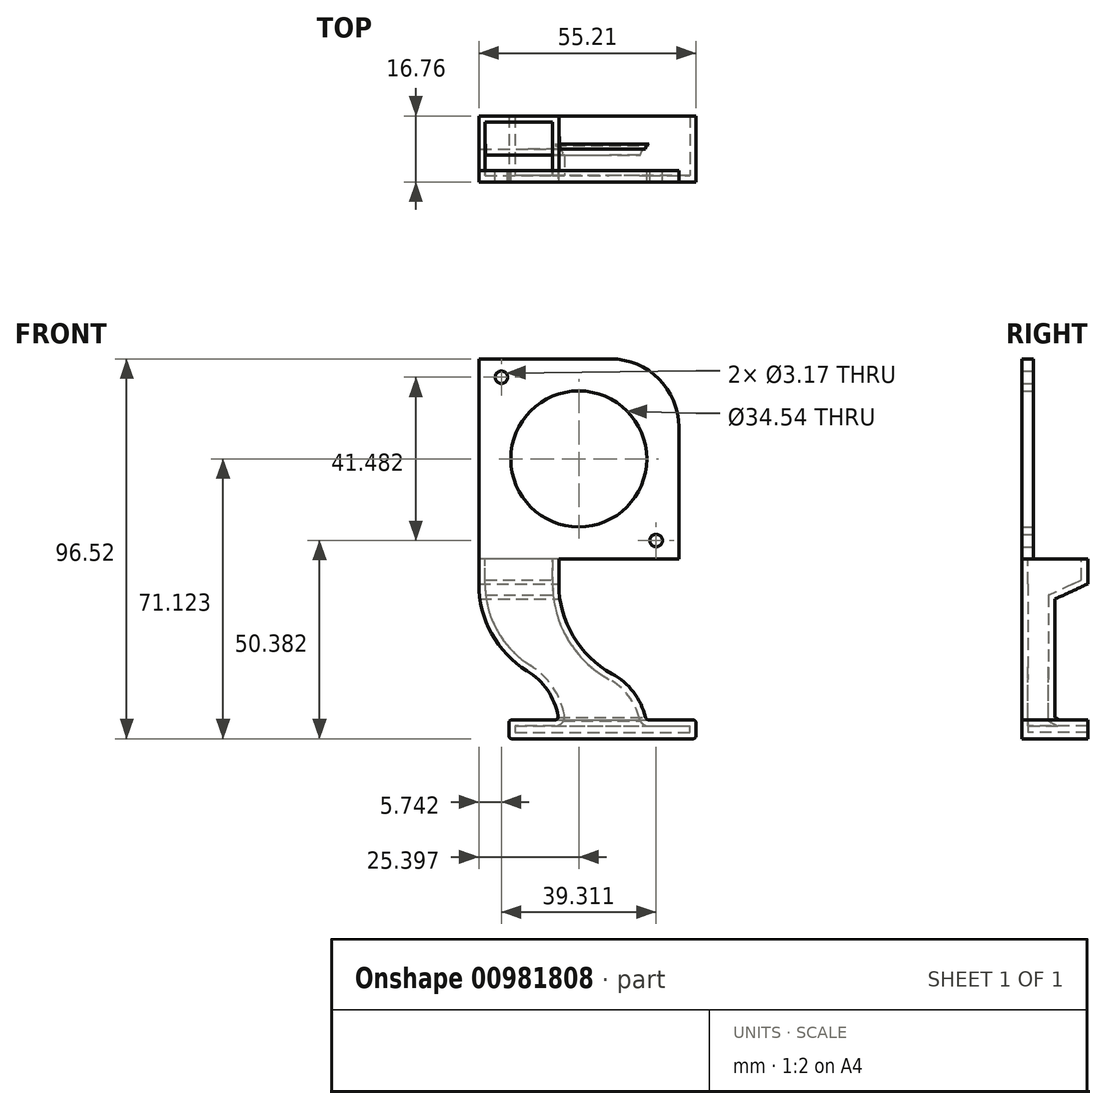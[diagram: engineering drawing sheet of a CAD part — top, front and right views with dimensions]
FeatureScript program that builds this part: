
annotation { "Feature Type Name" : "Feature", "Feature Type Description" : "" }
export const myFeature = defineFeature(function(context is Context, id is Id, definition is map)
    precondition{}
    {
        {
            var Q0;
            Q0=qCreatedBy(makeId("Front.planeOp"),FACE);
            var sketch = newSketch(context, id + "F0", { "sketchPlane" : qUnion([Q0])});
            skLineSegment(sketch, "E0", {"start": v(-842.3, 183.05) * mm, "end": v(-808.77, 183.05) * mm});
            skLineSegment(sketch, "E1", {"start": v(-791.5, 165.78) * mm, "end": v(-791.5, 132.25) * mm});
            skLineSegment(sketch, "E2", {"start": v(-791.5, 132.25) * mm, "end": v(-842.3, 132.25) * mm});
            skLineSegment(sketch, "E3", {"start": v(-842.3, 132.25) * mm, "end": v(-842.3, 183.05) * mm});
            skCircle(sketch, "E4", {"center": v(-816.9, 157.65) * mm, "radius": 17.27 * mm});
            skPoint(sketch, "E4.centerSnap0", {"position": v(-791.5, 157.65) * mm});
            skPoint(sketch, "E4.centerSnap1", {"position": v(-816.9, 132.25) * mm});
            skCircle(sketch, "E5", {"center": v(-836.56, 178.4) * mm, "radius": 1.59 * mm});
            skCircle(sketch, "E6", {"center": v(-797.25, 136.91) * mm, "radius": 1.59 * mm});
            skPoint(sketch, "E7.visualSharp", {"position": v(-791.5, 183.05) * mm});
            skArc(sketch, "E7.filletArc", {"start": v(-791.5, 165.78) * mm, "mid": v(-796.56, 178) * mm, "end": v(-808.77, 183.05) * mm});
            skSolve(sketch);
        }
        {
            var Q0;
            Q0 = qSketchRegion(id + "F0", true);
            extrude(context, id + "F1", {"entities" : qUnion([Q0]), "depth" : 2.92 * mm, "offsetDistance" : 25.4 * mm});
        }
        {
            var Q0;
            Q0=makeQuery(id+"F1.opExtrude","SWEPT_FACE",FACE,{"disambiguationData":[OSD([sQuery(id+"F0.wireOp",EDGE,"E3")])]});
            var sketch = newSketch(context, id + "F2", { "sketchPlane" : qUnion([Q0])});
            skLineSegment(sketch, "E8.bottom", {"start": v(2.92, 132.25) * mm, "end": v(-13.84, 132.25) * mm});
            skLineSegment(sketch, "E8.left", {"start": v(2.92, 132.25) * mm, "end": v(2.92, 125.9) * mm});
            skPoint(sketch, "E9.first.point", {"position": v(2.92, 125.9) * mm});
            skLineSegment(sketch, "E10", {"start": v(2.92, 125.9) * mm, "end": v(-13.84, 125.9) * mm});
            skLineSegment(sketch, "E11", {"start": v(-13.84, 125.9) * mm, "end": v(-13.84, 132.25) * mm});
            skSolve(sketch);
        }
        {
            var Q0;
            {var subQ0=sQuery(id+"F2.wireOp",EDGE,"E8.left");Q0=makeQuery(id+"F2.imprint","IMPRINT",FACE,{"disambiguationData":[TD([[makeQuery(id+"F2.imprint","IMPRINT",EDGE,{"derivedFrom":subQ0}),-1.0]])]});}
            extrude(context, id + "F3", {"entities" : qUnion([Q0]), "operationType" : NewBodyOperationType.ADD, "depth" : -20.32 * mm, "offsetDistance" : 25.4 * mm});
        }
        {
            var Q0;
            Q0=makeQuery(id+"F3.boolean.opBoolean","MERGE",FACE,{"derivedFrom":[makeQuery(id+"F1.opExtrude","CAP_FACE",FACE,{"disambiguationData":[OSD([sQuery(id+"F0.wireOp",EDGE,"E0"),sQuery(id+"F0.wireOp",EDGE,"E1"),sQuery(id+"F0.wireOp",EDGE,"E2"),sQuery(id+"F0.wireOp",EDGE,"E3"),sQuery(id+"F0.wireOp",EDGE,"E4"),sQuery(id+"F0.wireOp",EDGE,"E5"),sQuery(id+"F0.wireOp",EDGE,"E6"),sQuery(id+"F0.wireOp",EDGE,"E7.filletArc")])],"isStart":false}),makeQuery(id+"F3.opExtrude","SWEPT_FACE",FACE,{"disambiguationData":[OSD([sQuery(id+"F2.wireOp",EDGE,"E8.left")])]})]});
            var sketch = newSketch(context, id + "F4", { "sketchPlane" : qUnion([Q0])});
            skArc(sketch, "E12", {"start": v(-842.3, 125.9) * mm, "mid": v(-839.02, 113.25) * mm, "end": v(-830, 103.78) * mm});
            skArc(sketch, "E13", {"start": v(-821.98, 125.9) * mm, "mid": v(-818.34, 112.62) * mm, "end": v(-808.43, 103.06) * mm});
            skLineSegment(sketch, "E14", {"start": v(-821.98, 91.36) * mm, "end": v(-821.98, 90.34) * mm});
            skLineSegment(sketch, "E15", {"start": v(-799.8, 91.36) * mm, "end": v(-799.76, 91.2) * mm});
            skPoint(sketch, "E16.visualSharp", {"position": v(-821.98, 100.5) * mm});
            skArc(sketch, "E16.filletArc", {"start": v(-822.14, 92.35) * mm, "mid": v(-824.87, 98.89) * mm, "end": v(-830, 103.78) * mm});
            skPoint(sketch, "E17.visualSharp", {"position": v(-801.66, 100.5) * mm});
            skArc(sketch, "E17.filletArc", {"start": v(-799.94, 92) * mm, "mid": v(-803.02, 98.42) * mm, "end": v(-808.43, 103.06) * mm});
            skLineSegment(sketch, "E18", {"start": v(-822.96, 91.36) * mm, "end": v(-833.85, 91.36) * mm});
            skLineSegment(sketch, "E19", {"start": v(-799.13, 91.36) * mm, "end": v(-787.93, 91.36) * mm});
            skLineSegment(sketch, "E20", {"start": v(-787.93, 86.53) * mm, "end": v(-833.85, 86.53) * mm});
            skLineSegment(sketch, "E21", {"start": v(-834.68, 87.36) * mm, "end": v(-834.68, 90.53) * mm});
            skLineSegment(sketch, "E22", {"start": v(-787.1, 90.53) * mm, "end": v(-787.1, 87.36) * mm});
            skPoint(sketch, "E23.visualSharp", {"position": v(-821.98, 91.36) * mm});
            skArc(sketch, "E23.filletArc", {"start": v(-822.96, 91.36) * mm, "mid": v(-822.32, 91.66) * mm, "end": v(-822.14, 92.35) * mm});
            skPoint(sketch, "E24.visualSharp", {"position": v(-799.8, 91.36) * mm});
            skArc(sketch, "E24.filletArc", {"start": v(-799.94, 92) * mm, "mid": v(-799.64, 91.54) * mm, "end": v(-799.13, 91.36) * mm});
            skPoint(sketch, "E25.visualSharp", {"position": v(-787.1, 91.36) * mm});
            skArc(sketch, "E25.filletArc", {"start": v(-787.1, 90.53) * mm, "mid": v(-787.34, 91.12) * mm, "end": v(-787.93, 91.36) * mm});
            skPoint(sketch, "E26.visualSharp", {"position": v(-787.1, 86.53) * mm});
            skArc(sketch, "E26.filletArc", {"start": v(-787.93, 86.53) * mm, "mid": v(-787.34, 86.78) * mm, "end": v(-787.1, 87.36) * mm});
            skPoint(sketch, "E27.visualSharp", {"position": v(-834.68, 91.36) * mm});
            skArc(sketch, "E27.filletArc", {"start": v(-833.85, 91.36) * mm, "mid": v(-834.44, 91.12) * mm, "end": v(-834.68, 90.53) * mm});
            skPoint(sketch, "E28.visualSharp", {"position": v(-834.68, 86.53) * mm});
            skArc(sketch, "E28.filletArc", {"start": v(-834.68, 87.36) * mm, "mid": v(-834.44, 86.78) * mm, "end": v(-833.85, 86.53) * mm});
            skLineSegment(sketch, "E29", {"start": v(-842.3, 125.9) * mm, "end": v(-821.98, 125.9) * mm});
            skSolve(sketch);
        }
        {
            var Q0;
            Q0=makeQuery(id+"F4.imprint","IMPRINT",FACE,{"disambiguationData":[TD([[makeQuery(id+"F4.imprint","IMPRINT",EDGE,{"derivedFrom":sQuery(id+"F4.wireOp",EDGE,"E12")}),1.0]])]});
            var Q1;
            Q1=makeQuery(id+"F3.opExtrude","SWEPT_FACE",FACE,{"disambiguationData":[OSD([sQuery(id+"F2.wireOp",EDGE,"E11")])]});
            extrude(context, id + "F5", {"entities" : qUnion([Q0]), "operationType" : NewBodyOperationType.ADD, "endBound" : BoundingType.UP_TO_SURFACE, "oppositeDirection" : true, "depth" : 25.4 * mm, "endBoundEntityFace" : qUnion([Q1]), "offsetDistance" : 25.4 * mm});
        }
        {
            var Q0;
            Q0=makeQuery(id+"F5.opExtrude","SWEPT_FACE",FACE,{"disambiguationData":[OSD([sQuery(id+"F4.wireOp",EDGE,"E22")])]});
            var sketch = newSketch(context, id + "F6", { "sketchPlane" : qUnion([Q0])});
            skLineSegment(sketch, "E30", {"start": v(13.84, 125.9) * mm, "end": v(5.46, 122) * mm});
            skLineSegment(sketch, "E31", {"start": v(5.46, 122) * mm, "end": v(5.46, 92) * mm});
            skLineSegment(sketch, "E32", {"start": v(5.46, 92) * mm, "end": v(6.65, 91.36) * mm});
            skLineSegment(sketch, "E33", {"start": v(6.65, 91.36) * mm, "end": v(13.84, 91.36) * mm});
            skLineSegment(sketch, "E34", {"start": v(13.84, 125.9) * mm, "end": v(13.84, 90.53) * mm});
            skSolve(sketch);
        }
        {
            var Q0;
            Q0 = qSketchRegion(id + "F6", true);
            var Q1;
            Q1=makeQuery(id+"F3.boolean.opBoolean","MERGE",FACE,{"derivedFrom":[makeQuery(id+"F1.opExtrude","SWEPT_FACE",FACE,{"disambiguationData":[OSD([sQuery(id+"F0.wireOp",EDGE,"E3")])]}),makeQuery(id+"F3.opExtrude","CAP_FACE",FACE,{"disambiguationData":[OSD([sQuery(id+"F2.wireOp",EDGE,"E8.bottom"),sQuery(id+"F2.wireOp",EDGE,"E8.left"),sQuery(id+"F2.wireOp",EDGE,"E10"),sQuery(id+"F2.wireOp",EDGE,"E11")])],"isStart":true})]});
            extrude(context, id + "F7", {"entities" : qUnion([Q0]), "operationType" : NewBodyOperationType.REMOVE, "endBound" : BoundingType.UP_TO_SURFACE, "oppositeDirection" : true, "depth" : 25.4 * mm, "endBoundEntityFace" : qUnion([Q1]), "offsetDistance" : 25.4 * mm});
        }
        {
            var Q0;
            Q0=makeQuery(id+"F3.opExtrude","SWEPT_FACE",FACE,{"disambiguationData":[OSD([sQuery(id+"F2.wireOp",EDGE,"E8.bottom")])]});
            var Q1;
            {var subQ0=sQuery(id+"F4.wireOp",EDGE,"E22");var subQ1=sQuery(id+"F4.wireOp",EDGE,"E21");var subQ2=sQuery(id+"F4.wireOp",EDGE,"E25.filletArc");var subQ3=sQuery(id+"F4.wireOp",EDGE,"E20");var subQ4=sQuery(id+"F4.wireOp",EDGE,"E26.filletArc");var subQ5=sQuery(id+"F4.wireOp",EDGE,"E27.filletArc");var subQ6=sQuery(id+"F4.wireOp",EDGE,"E28.filletArc");Q1=makeQuery(id+"F7.boolean.opBoolean","SPLIT",FACE,{"disambiguationData":[TD([makeQuery(id+"F5.opExtrude","SWEPT_FACE",FACE,{"disambiguationData":[OSD([subQ3])]})])],"derivedFrom":makeQuery(id+"F5.boolean.opBoolean","MERGE",FACE,{"derivedFrom":[makeQuery(id+"F3.opExtrude","SWEPT_FACE",FACE,{"disambiguationData":[OSD([sQuery(id+"F2.wireOp",EDGE,"E11")])]}),makeQuery(id+"F5.opExtrude","CAP_FACE",FACE,{"disambiguationData":[OSD([sQuery(id+"F4.wireOp",EDGE,"E12"),sQuery(id+"F4.wireOp",EDGE,"E13"),sQuery(id+"F4.wireOp",EDGE,"E16.filletArc"),sQuery(id+"F4.wireOp",EDGE,"E17.filletArc"),sQuery(id+"F4.wireOp",EDGE,"E18"),sQuery(id+"F4.wireOp",EDGE,"E19"),subQ3,subQ1,subQ0,sQuery(id+"F4.wireOp",EDGE,"E23.filletArc"),sQuery(id+"F4.wireOp",EDGE,"E24.filletArc"),subQ2,subQ4,subQ5,subQ6,sQuery(id+"F4.wireOp",EDGE,"E29")])],"isStart":false})]})});}
            shell(context, id + "F8", {"entities" : qUnion([Q0, Q1]), "thickness" : 1.59 * mm});
        }
    });
